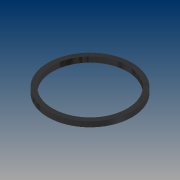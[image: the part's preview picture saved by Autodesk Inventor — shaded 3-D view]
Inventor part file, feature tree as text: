
AUTODESK INVENTOR PART (.ipt)
format: ipt  version: 2015 (Build 190159000, 159)  size: 78,336 bytes
history: native  units: mm
features: extrude x1, sketch x1
ambient origin geometry x8: Origin, YZ Plane, XZ Plane, XY Plane, X Axis, Y Axis, Z Axis, Center Point
bodies: Solid1 (feature_tree)
feature tree (2):
  extrude  "Extrusion1"  Depth=5.0mm
  sketch  "Sketch1"  dims[d0=80.0mm d1=71.0mm d2=5.0mm d3=0.0mm]
